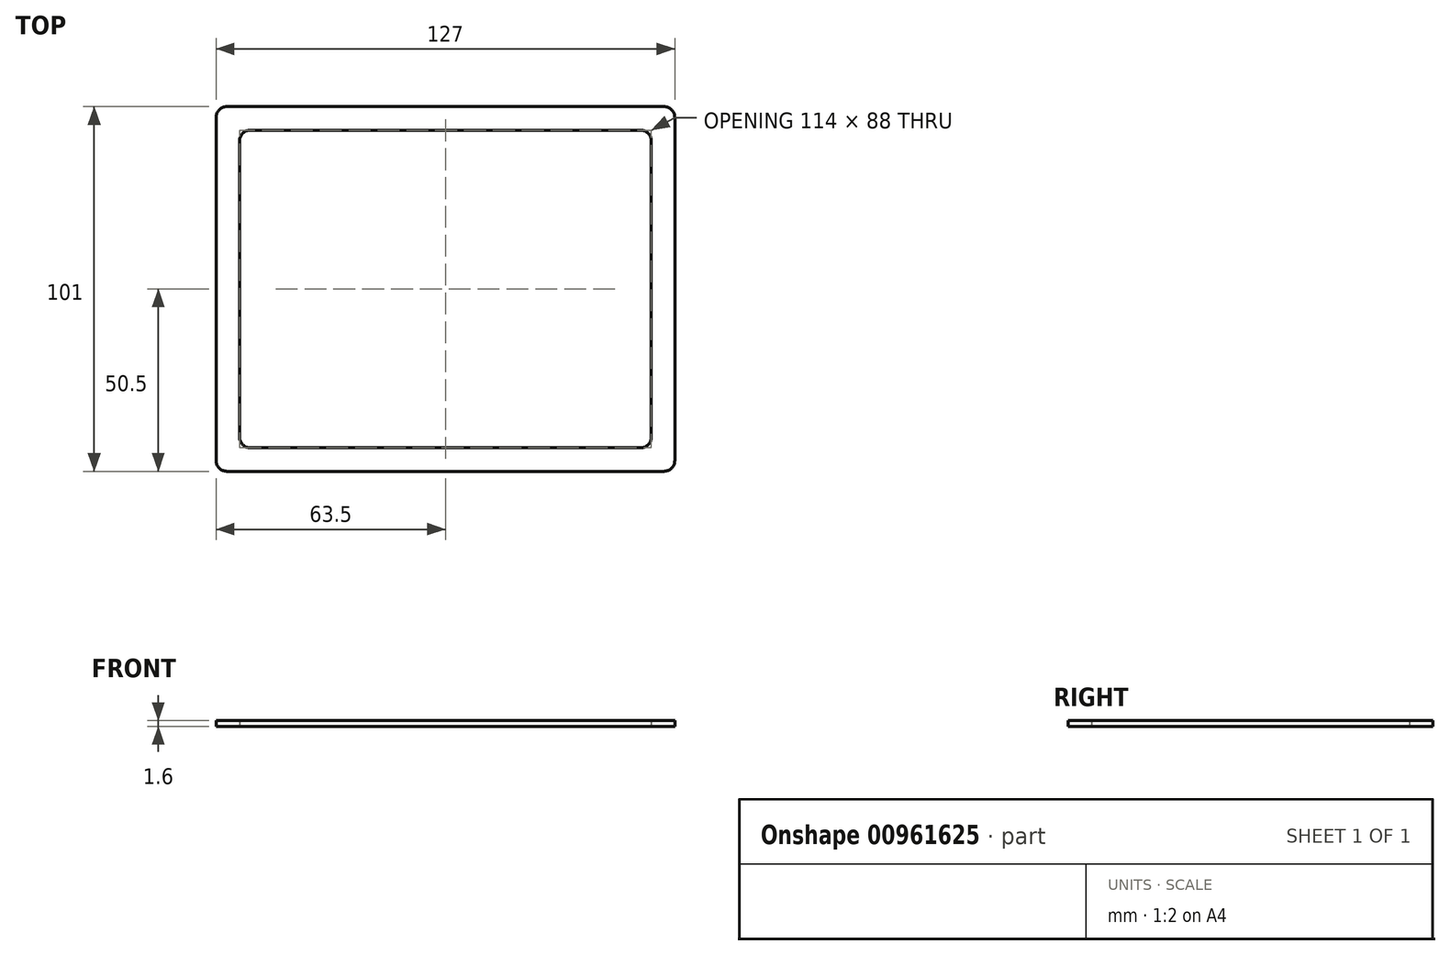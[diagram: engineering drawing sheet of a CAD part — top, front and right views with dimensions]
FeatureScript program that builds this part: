
annotation { "Feature Type Name" : "Feature", "Feature Type Description" : "" }
export const myFeature = defineFeature(function(context is Context, id is Id, definition is map)
    precondition{}
    {
        {
            var Q0;
            Q0=qCreatedBy(makeId("Top.planeOp"),FACE);
            var sketch = newSketch(context, id + "F0", { "sketchPlane" : qUnion([Q0])});
            skLineSegment(sketch, "E0.bottom", {"start": v(63.5, -50.5) * mm, "end": v(-63.5, -50.5) * mm});
            skLineSegment(sketch, "E0.top", {"start": v(63.5, 50.5) * mm, "end": v(-63.5, 50.5) * mm});
            skLineSegment(sketch, "E0.left", {"start": v(63.5, -50.5) * mm, "end": v(63.5, 50.5) * mm});
            skLineSegment(sketch, "E0.right", {"start": v(-63.5, -50.5) * mm, "end": v(-63.5, 50.5) * mm});
            skPoint(sketch, "E0.middle", {"position": v(0, 0) * mm});
            skPoint(sketch, "E1", {"position": v(-57, 44) * mm});
            skLineSegment(sketch, "E2.bottom", {"start": v(-57, 44) * mm, "end": v(57, 44) * mm});
            skLineSegment(sketch, "E2.top", {"start": v(-57, -44) * mm, "end": v(57, -44) * mm});
            skLineSegment(sketch, "E2.left", {"start": v(-57, 44) * mm, "end": v(-57, -44) * mm});
            skLineSegment(sketch, "E2.right", {"start": v(57, 44) * mm, "end": v(57, -44) * mm});
            skSolve(sketch);
        }
        {
            var Q0;
            Q0=qSketchRegion(id+"F0",true);
            extrude(context, id + "F1", {"entities" : qUnion([Q0]), "depth" : 1.6 * mm, "offsetDistance" : 25 * mm});
        }
        {
            var Q0;
            Q0=makeQuery(id+"F1.opExtrude","SWEPT_EDGE",EDGE,{"disambiguationData":[OSD([sQuery(id+"F0.wireOp",EDGE,"E0.bottom"),sQuery(id+"F0.wireOp",EDGE,"E0.right")])]});
            var Q1;
            Q1=makeQuery(id+"F1.opExtrude","SWEPT_EDGE",EDGE,{"disambiguationData":[OSD([sQuery(id+"F0.wireOp",EDGE,"E0.bottom"),sQuery(id+"F0.wireOp",EDGE,"E0.left")])]});
            var Q2;
            Q2=makeQuery(id+"F1.opExtrude","SWEPT_EDGE",EDGE,{"disambiguationData":[OSD([sQuery(id+"F0.wireOp",EDGE,"E0.top"),sQuery(id+"F0.wireOp",EDGE,"E0.left")])]});
            var Q3;
            Q3=makeQuery(id+"F1.opExtrude","SWEPT_EDGE",EDGE,{"disambiguationData":[OSD([sQuery(id+"F0.wireOp",EDGE,"E2.bottom"),sQuery(id+"F0.wireOp",EDGE,"E2.left")])]});
            var Q4;
            Q4=makeQuery(id+"F1.opExtrude","SWEPT_EDGE",EDGE,{"disambiguationData":[OSD([sQuery(id+"F0.wireOp",EDGE,"E2.top"),sQuery(id+"F0.wireOp",EDGE,"E2.left")])]});
            var Q5;
            Q5=makeQuery(id+"F1.opExtrude","SWEPT_EDGE",EDGE,{"disambiguationData":[OSD([sQuery(id+"F0.wireOp",EDGE,"E2.top"),sQuery(id+"F0.wireOp",EDGE,"E2.right")])]});
            var Q6;
            Q6=makeQuery(id+"F1.opExtrude","SWEPT_EDGE",EDGE,{"disambiguationData":[OSD([sQuery(id+"F0.wireOp",EDGE,"E0.top"),sQuery(id+"F0.wireOp",EDGE,"E0.right")])]});
            var Q7;
            Q7=makeQuery(id+"F1.opExtrude","SWEPT_EDGE",EDGE,{"disambiguationData":[OSD([sQuery(id+"F0.wireOp",EDGE,"E2.bottom"),sQuery(id+"F0.wireOp",EDGE,"E2.right")])]});
            fillet(context, id + "F2", {"entities" : qUnion([Q0, Q1, Q2, Q3, Q4, Q5, Q6, Q7]), "radius" : 3 * mm, "tangentPropagation" : true, "allowEdgeOverflow" : false});
        }
    });
